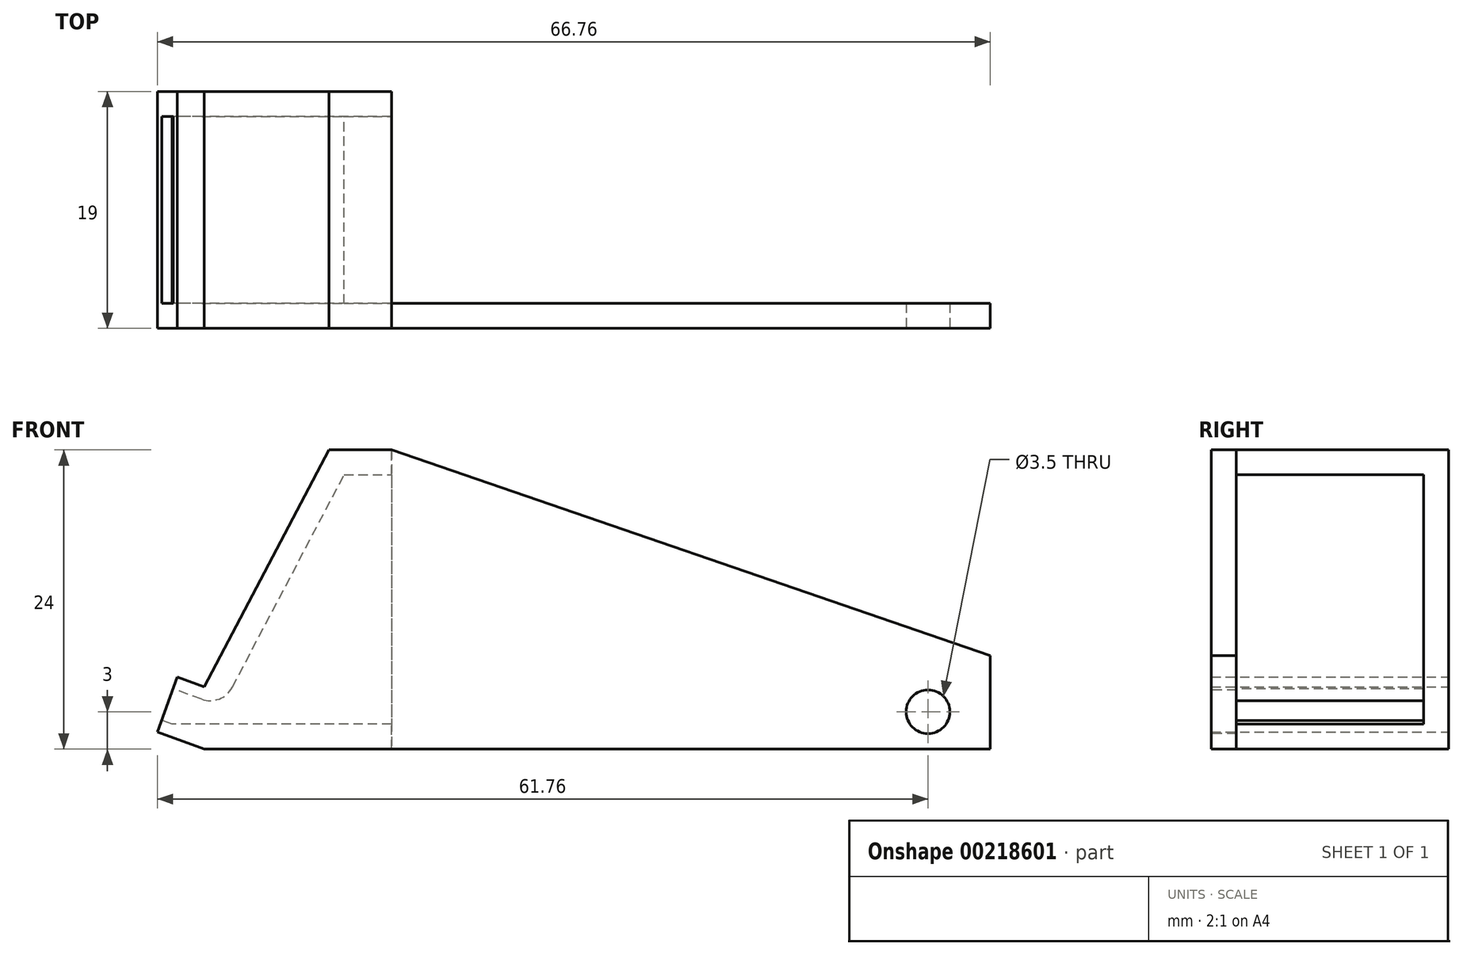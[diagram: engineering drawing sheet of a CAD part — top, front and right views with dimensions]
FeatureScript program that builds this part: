
annotation { "Feature Type Name" : "Feature", "Feature Type Description" : "" }
export const myFeature = defineFeature(function(context is Context, id is Id, definition is map)
    precondition{}
    {
        {
            var Q0;
            Q0=qCreatedBy(makeId("Front.planeOp"),FACE);
            var sketch = newSketch(context, id + "F0", { "sketchPlane" : qUnion([Q0])});
            skLineSegment(sketch, "E0", {"start": v(0, 5) * mm, "end": v(10, 24) * mm});
            skLineSegment(sketch, "E1", {"start": v(10, 24) * mm, "end": v(15, 24) * mm});
            skLineSegment(sketch, "E2", {"start": v(15, 24) * mm, "end": v(15, 0) * mm});
            skLineSegment(sketch, "E3", {"start": v(15, 0) * mm, "end": v(0, 0) * mm});
            skLineSegment(sketch, "E4", {"start": v(0, 0) * mm, "end": v(-3.76, 1.37) * mm});
            skLineSegment(sketch, "E5", {"start": v(-3.76, 1.37) * mm, "end": v(-2.15, 5.78) * mm});
            skLineSegment(sketch, "E6", {"start": v(-2.15, 5.78) * mm, "end": v(0, 5) * mm});
            skSolve(sketch);
        }
        {
            var Q0;
            Q0 = qSketchRegion(id + "F0", true);
            extrude(context, id + "F1", {"entities" : qUnion([Q0]), "depth" : 19 * mm, "offsetDistance" : 25 * mm, "symmetric" : true});
        }
        {
            var Q0;
            Q0=makeQuery(id+"F1.opExtrude","SWEPT_FACE",FACE,{"disambiguationData":[OSD([sQuery(id+"F0.wireOp",EDGE,"E2")])]});
            shell(context, id + "F2", {"entities" : qUnion([Q0]), "thickness" : 2 * mm});
        }
        {
            var Q0;
            Q0=makeQuery(id+"F1.opExtrude","CAP_FACE",FACE,{"disambiguationData":[OSD([sQuery(id+"F0.wireOp",EDGE,"ycq5FEmf-DA3U-3vHs-K8Da-K1XGNjrIITK1"),sQuery(id+"F0.wireOp",EDGE,"E0"),sQuery(id+"F0.wireOp",EDGE,"E1"),sQuery(id+"F0.wireOp",EDGE,"E2"),sQuery(id+"F0.wireOp",EDGE,"E3")])],"isStart":false});
            var sketch = newSketch(context, id + "F3", { "sketchPlane" : qUnion([Q0])});
            skLineSegment(sketch, "E7", {"start": v(15, 24) * mm, "end": v(15, 0) * mm});
            skLineSegment(sketch, "E8", {"start": v(15, 0) * mm, "end": v(63, 0) * mm});
            skLineSegment(sketch, "E9", {"start": v(63, 0) * mm, "end": v(63, 7.5) * mm});
            skCircle(sketch, "E10", {"center": v(58, 3) * mm, "radius": 1.75 * mm});
            skLineSegment(sketch, "E11", {"start": v(15, 24) * mm, "end": v(63, 7.5) * mm});
            skSolve(sketch);
        }
        {
            var Q0;
            Q0 = qSketchRegion(id + "F3", true);
            var Q1;
            {var subQ0=sQuery(id+"F0.wireOp",EDGE,"ycq5FEmf-DA3U-3vHs-K8Da-K1XGNjrIITK1");var subQ1=sQuery(id+"F0.wireOp",EDGE,"E3");var subQ2=sQuery(id+"F0.wireOp",EDGE,"E2");var subQ3=sQuery(id+"F0.wireOp",EDGE,"E1");var subQ4=sQuery(id+"F0.wireOp",EDGE,"E0");Q1=makeQuery(id+"FGGGnZ9MlOxDA5B_1.boolean.opBoolean","MERGE",FACE,{"derivedFrom":[makeQuery(id+"F2.opShell","OFFSET_FACE",FACE,{"disambiguationData":[OSD([subQ0,subQ4,subQ3,subQ2,subQ1]),TDD([makeQuery(id+"F1.opExtrude","CAP_FACE",FACE,{"disambiguationData":[OSD([subQ0,subQ4,subQ3,subQ2,subQ1])],"isStart":false})])]}),makeQuery(id+"FGGGnZ9MlOxDA5B_1.opExtrude","SWEPT_FACE",FACE,{"disambiguationData":[OSD([subQ0]),TDD([makeQuery(id+"F2.opShell","OFFSET_EDGE",EDGE,{"disambiguationData":[OSD([subQ0]),TDD([makeQuery(id+"F1.opExtrude","CAP_EDGE",EDGE,{"disambiguationData":[OSD([subQ0])],"isStart":false})])]})])]})]});}
            extrude(context, id + "F4", {"entities" : qUnion([Q0]), "operationType" : NewBodyOperationType.ADD, "endBound" : BoundingType.UP_TO_SURFACE, "oppositeDirection" : true, "depth" : 25 * mm, "endBoundEntityFace" : qUnion([Q1]), "offsetDistance" : 25 * mm});
        }
        {
            var Q0;
            Q0=makeQuery(id+"F1.opExtrude","SWEPT_FACE",FACE,{"disambiguationData":[OSD([sQuery(id+"F0.wireOp",EDGE,"E5")])]});
            var sketch = newSketch(context, id + "F5", { "sketchPlane" : qUnion([Q0])});
            skLineSegment(sketch, "E12.bottom", {"start": v(-7.5, 3.7) * mm, "end": v(7.5, 3.7) * mm});
            skLineSegment(sketch, "E12.top", {"start": v(-7.5, 1) * mm, "end": v(7.5, 1) * mm});
            skLineSegment(sketch, "E12.left", {"start": v(-7.5, 3.7) * mm, "end": v(-7.5, 1) * mm});
            skLineSegment(sketch, "E12.right", {"start": v(7.5, 3.7) * mm, "end": v(7.5, 1) * mm});
            skSolve(sketch);
        }
        {
            var Q0;
            Q0 = qSketchRegion(id + "F5", true);
            var Q1;
            Q1=makeQuery(id+"F2.opShell","OFFSET_FACE",FACE,{"disambiguationData":[OSD([sQuery(id+"F0.wireOp",EDGE,"E3")])]});
            extrude(context, id + "F6", {"entities" : qUnion([Q0]), "operationType" : NewBodyOperationType.REMOVE, "endBound" : BoundingType.UP_TO_SURFACE, "oppositeDirection" : true, "depth" : 25 * mm, "endBoundEntityFace" : qUnion([Q1]), "offsetDistance" : 25 * mm});
        }
        {
            var Q0;
            Q0=makeQuery(id+"F6.boolean.opBoolean","INTERSECT",EDGE,{"derivedFrom":[makeQuery(id+"F2.opShell","OFFSET_FACE",FACE,{"disambiguationData":[OSD([sQuery(id+"F0.wireOp",EDGE,"E0")])]}),makeQuery(id+"F6.opExtrude","SWEPT_FACE",FACE,{"disambiguationData":[OSD([sQuery(id+"F5.wireOp",EDGE,"E12.bottom")])]})]});
            fillet(context, id + "F7", {"entities" : qUnion([Q0]), "radius" : 2 * mm, "tangentPropagation" : true, "allowEdgeOverflow" : false});
        }
    });
